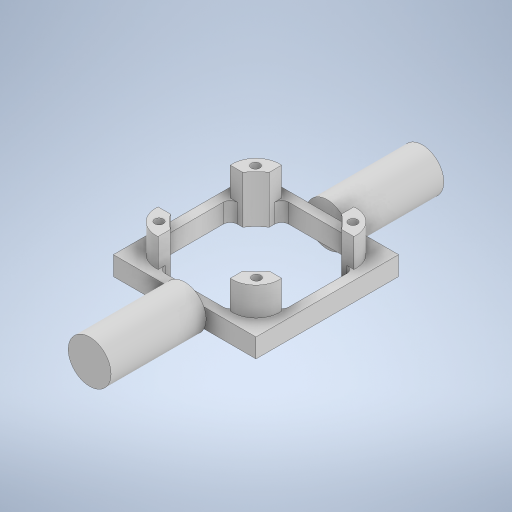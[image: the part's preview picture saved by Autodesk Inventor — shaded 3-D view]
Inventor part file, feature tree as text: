
AUTODESK INVENTOR PART (.ipt)
format: ipt  version: 2024 (Build 280153000, 153)  size: 431,104 bytes
history: native  units: in
note: dims shown in document units (in); Inventor stores cm internally (conversion verified against a paired STEP export)
features: extrude x8, sketch x8, fillet x1
ambient origin geometry x8: Origin, YZ Plane, XZ Plane, XY Plane, X Axis, Y Axis, Z Axis, Center Point
bodies: Solid1 (feature_tree)
feature tree (17):
  extrude  "Extrusion1"  Depth=3.937in TaperAngle=0.0deg
  sketch  "Sketch2"  dims[d3=1.378in d32=5.9055in]
  extrude  "Extrusion5"  Depth=5.9055in
  extrude  "Extrusion8"  Depth=5.9055in TaperAngle=0.0deg
  extrude  "Extrusion10"  Depth=5.1181in
  extrude  "Extrusion11"  Depth=5.1181in
  extrude  "Extrusion12"  Depth=0.7874in TaperAngle=0.0deg
  extrude  "Extrusion13"  Depth=1.4961in
  extrude  "Extrusion14"  Depth=0.3in
  fillet  "Fillet7"  Radius=1.4961in
  sketch  "Sketch1"  dims[d0=1.7717in d1=3.937in d2=0.0in]
  sketch  "Sketch5"  dims[d33=0.7874in d34=5.9055in d35=0.0in]
  sketch  "Sketch8"  dims[d59=3.937in d60=0.0in d72=5.1181in]
  sketch  "Sketch11"  dims[d73=5.1181in d74=2.9528in]
  sketch  "Sketch12"  dims[d75=2.9528in d80=0.7874in d81=0.0in]
  sketch  "Sketch13"  dims[d84=1.4961in d85=1.4961in]
  sketch  "Sketch14"  dims[d86=0.5118in d87=1.4961in d88=1.4961in d89=0.5118in d90=2.5315in d91=0.3543in d92=0.5026in d93=0.5407in d94=1.9685in d95=0.0in d96=1.4961in d97=1.4961in d98=1.4961in d99=1.4961in d100=0.5118in d101=0.5118in d102=0.5118in d103=0.5118in d104=0.5118in d105=0.5118in d106=2.5315in d107=2.5315in d108=2.5315in d109=0.3543in d110=0.3543in d111=0.3543in d112=0.5026in d113=0.5407in d114=0.5026in d115=0.5407in d116=0.5407in d117=0.5026in d118=0.9843in d119=0.9843in d120=0.9843in d121=0.9843in d122=2.5315in d125=2.5315in d126=2.5315in d127=2.5315in d128=1.1811in d129=0.0in d130=0.3543in d131=0.3543in d132=0.3543in d133=0.3543in d134=3.937in d135=0.0in d136=1.7717in d144=2.9921in d145=0.0in d148=0.3in d28=0.0in d29=0.0in d30=0.0in d31=0.0in d146=0.0197in d147=0.0344in]
